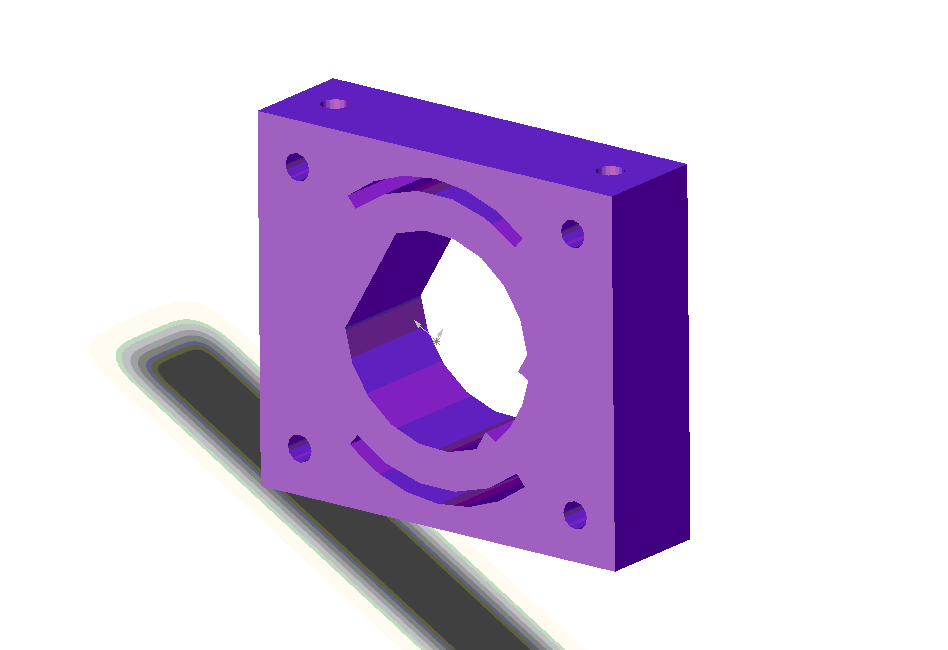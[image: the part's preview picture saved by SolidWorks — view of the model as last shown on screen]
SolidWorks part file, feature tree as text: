
SOLIDWORKS PART (.sldprt)
format: sldprt  version: not decoded by parser v0  size: 125,440 bytes
history: native  units: mm
features: sketch x4, cut_extrude x3, extrude x1 (+8 scaffold rows collapsed)
feature tree (16):
  scaffold x8  (default folders/planes/origin — collapsed)
  sketch  "Sketch1"  dims[c1.D6=29.5mm c1.D9=3.7mm c1.D10=30.0mm c1.D1=28.575mm c1.D2=57.15mm c1.D3=25.4mm c1.D4=50.8mm c1.D5=~16.632498mm c2.D5=30.0deg c2.D7=0.15mm c2.D8=0.15mm c2.D9=5.4mm c2.D11=10.8mm]
  extrude  "Base-Extrude"  Depth=15.875mm
  sketch  "Sketch2"  dims[D9=3.8mm D10=3.8mm D11=3.8mm D12=3.8mm D1=6.35mm D2=6.35mm D3=6.35mm D4=6.35mm D5=6.35mm D6=6.35mm D7=6.35mm D8=6.35mm]
  cut_extrude  "Cut-Extrude1"  [1 undecoded]
  sketch  "Sketch3"  dims[D5=3.8mm D6=3.8mm D1=6.35mm D2=6.35mm D3=7.9375mm D4=7.9375mm]
  cut_extrude  "Cut-Extrude2"  [1 undecoded]
  sketch  "Sketch5"  dims[c1.D1=44.0mm c1.D2=40.0mm c1.D3=57.15mm c2.D3=50.0deg c2.D4=~42.966735mm c3.D4=50.0deg c3.D5=57.15mm c4.D5=50.0deg c4.D6=57.15mm c5.D6=50.0deg]
  cut_extrude  "Cut-Extrude3"  [1 undecoded]
decode coverage: 5 of 8 modeling features carry decoded parameters
note: ~ marks probable driven/reference dimensions
note: 3 parameter values undecoded
summary: no parameter record found for 3 features
note: suppression state not decoded; provenance and decode notes live in map.json
